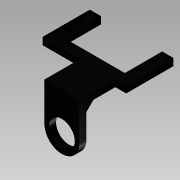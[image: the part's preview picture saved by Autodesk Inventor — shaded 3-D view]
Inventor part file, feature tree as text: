
AUTODESK INVENTOR PART (.ipt)
format: ipt  version: 2015 SP1 (Build 190203100, 203)  size: 288,768 bytes
history: native  units: mm
features: extrude x12, sketch x11, projected_geometry x4, plane x2, mirror x1
ambient origin geometry x8: Origin, YZ Plane, XZ Plane, XY Plane, X Axis, Y Axis, Z Axis, Center Point
bodies: Solid1 (feature_tree)
feature tree (30):
  sketch  "Sketch1"  dims[d19=3.0mm d20=0.0mm d22=39.4615mm]
  extrude  "Extrusion1"  Depth=39.4615mm
  plane  "Work Plane1"
  extrude  "Extrusion2"  Depth=24.75mm TaperAngle=0.0deg
  extrude  "Extrusion3"  Depth=24.75mm
  extrude  "Extrusion4"  Depth=4.980307mm
  extrude  "Extrusion5"  Depth=10.0mm TaperAngle=0.0deg
  extrude  "Extrusion6"  Depth=2.0mm
  extrude  "Extrusion7"  Depth=5.0mm TaperAngle=0.0deg
  extrude  "Extrusion8"  Depth=5.0mm TaperAngle=0.0deg
  extrude  "Extrusion9"  Depth=1.0mm
  mirror  "Mirror1"
  extrude  "Extrusion10"  TaperAngle=0.0deg  [1 undecoded]
  extrude  "Extrusion11"  Depth=5.0mm
  plane  "Work Plane2"
  sketch  "Sketch12"  dims[d64=7.0mm d65=6.460614mm d66=5.0mm d67=0.0mm d68=7.974mm d69=5.0mm d70=5.0mm d71=0.0mm d72=59.16mm d73=5.0mm d74=0.0mm d75=2.0mm d76=0.0mm d78=-9.545mm d79=5.0mm d80=45.0deg d81=24.75mm d82=0.0mm d83=5.0mm]
  extrude  "Extrusion12"  Depth=5.0mm TaperAngle=0.0deg
  sketch  "Sketch2"  dims[d23=18.25mm d24=24.75mm d25=24.75mm d26=25.0mm d27=25.0mm d32=3.0mm d33=0.0mm]
  sketch  "Sketch3"  dims[d38=90.0deg d39=24.75mm]
  projected_geometry  "Projected Loop1"
  projected_geometry  "Projected Loop2"
  sketch  "Sketch4"  dims[d41=90.0deg d42=4.980307mm d43=4.980307mm]
  projected_geometry  "Projected Loop3"
  sketch  "Sketch5"  dims[d44=4.980307mm d45=4.980307mm d46=10.0mm d47=0.0mm]
  sketch  "Sketch6"  dims[d50=2.0mm d51=0.0mm d52=2.0mm]
  sketch  "Sketch7"  dims[d53=2.0mm d54=5.0mm d55=0.0mm]
  sketch  "Sketch8"  dims[d56=1.0mm d57=5.0mm d58=0.0mm]
  sketch  "Sketch9"  dims[d59=1.0mm d60=1.0mm]
  sketch  "Sketch10"  dims[d61=0.0mm d62=0.0mm d63=0.0mm]
  projected_geometry  "Projected Loop4"
note: 1 required parameter value undecoded (feature->parameter linkage not recoverable at this tier; creation-order binding heuristic only, values carry confidence <= 0.55)
